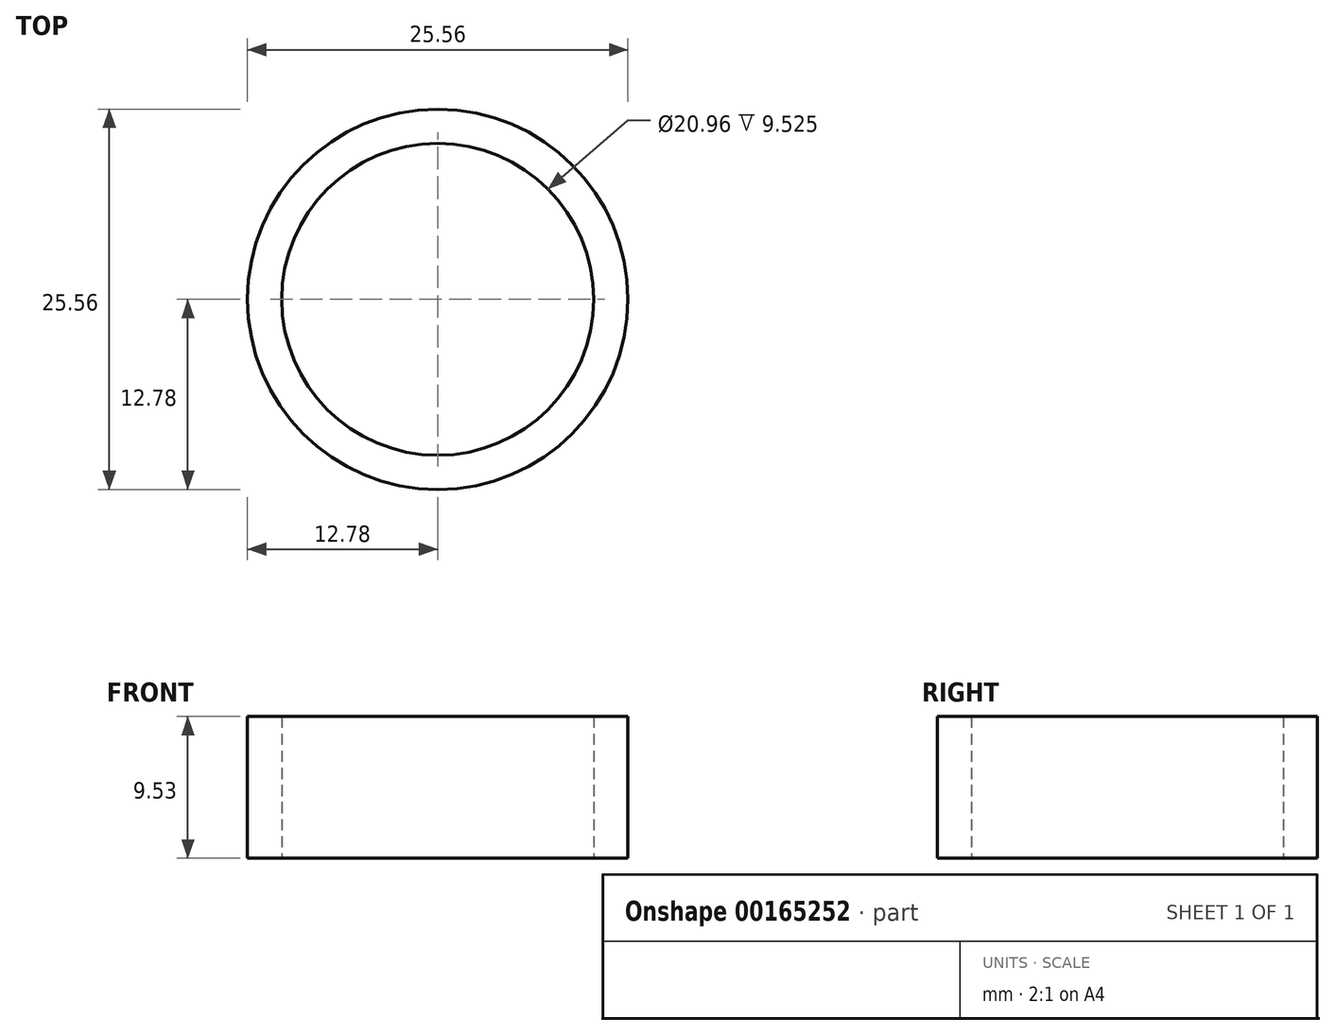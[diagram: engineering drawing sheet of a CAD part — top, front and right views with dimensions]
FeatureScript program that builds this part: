
annotation { "Feature Type Name" : "Feature", "Feature Type Description" : "" }
export const myFeature = defineFeature(function(context is Context, id is Id, definition is map)
    precondition{}
    {
        {
            var Q0;
            Q0=qCreatedBy(makeId("Top.planeOp"),FACE);
            var sketch = newSketch(context, id + "F0", { "sketchPlane" : qUnion([Q0])});
            skCircle(sketch, "E0", {"center": v(0, 0) * mm, "radius": 10.48 * mm});
            skCircle(sketch, "E1", {"center": v(0, 0) * mm, "radius": 12.78 * mm});
            skSolve(sketch);
        }
        {
            var Q0;
            Q0 = qSketchRegion(id + "F0", true);
            extrude(context, id + "F1", {"entities" : qUnion([Q0]), "depth" : 9.52 * mm});
        }
    });
